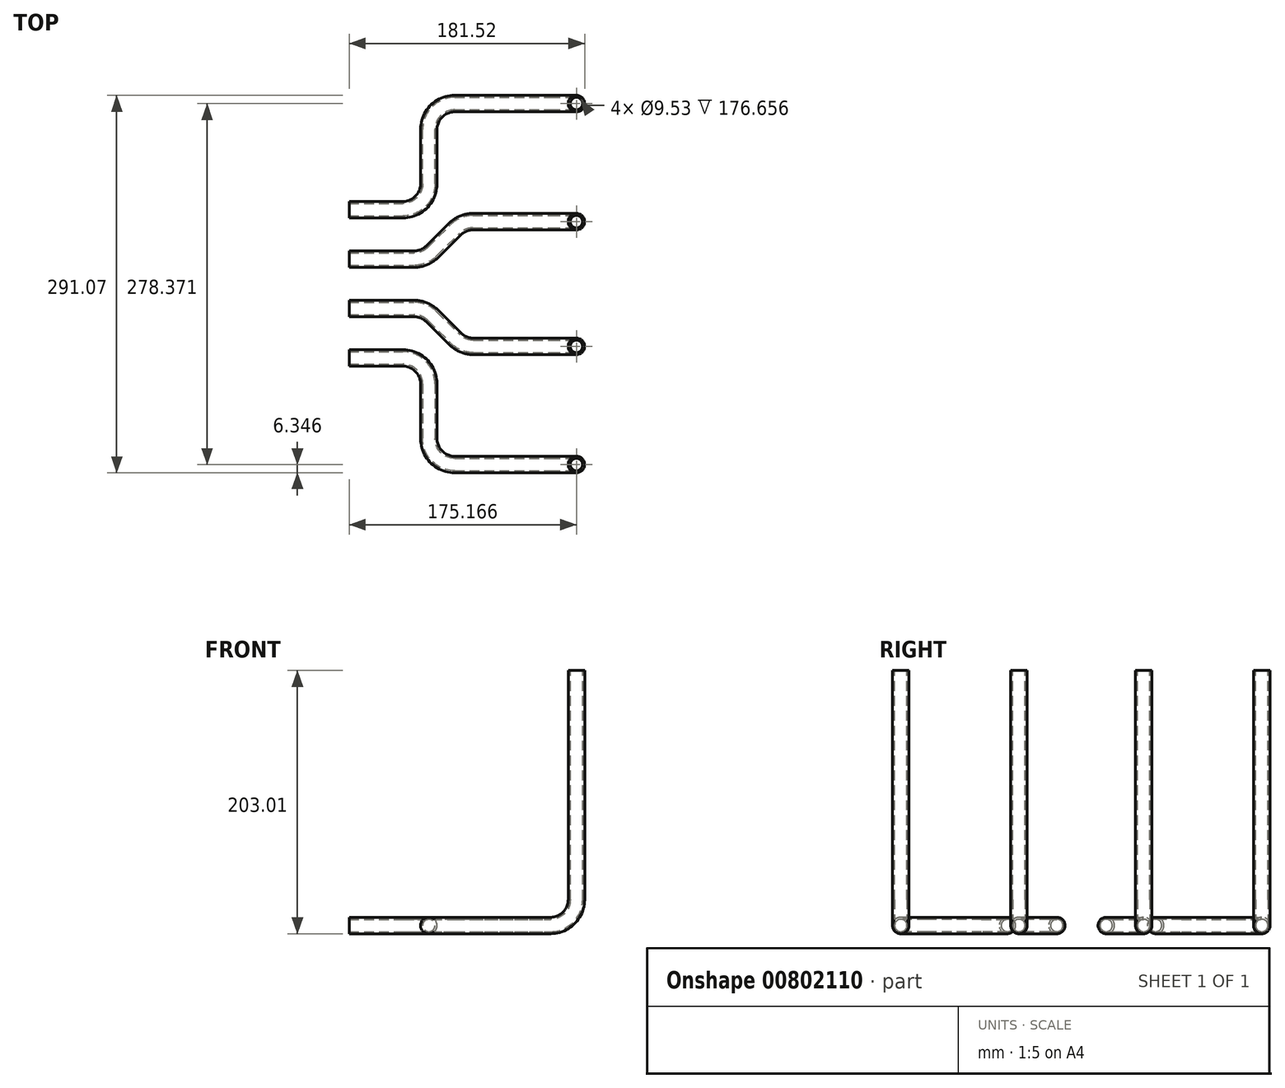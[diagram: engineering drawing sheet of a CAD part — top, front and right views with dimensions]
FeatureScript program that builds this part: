
annotation { "Feature Type Name" : "Feature", "Feature Type Description" : "" }
export const myFeature = defineFeature(function(context is Context, id is Id, definition is map)
    precondition{}
    {
        {
            var Q0;
            Q0=qCreatedBy(makeId("Front.planeOp"),FACE);
            cPlane(context, id + "F0", {"entities" : qUnion([Q0]), "cplaneType" : CPlaneType.OFFSET, "offset" : 158.4 * mm, "width" : 150 * mm, "height" : 150 * mm});
        }
        {
            var Q0;
            Q0=qCreatedBy(makeId("Top.planeOp"),FACE);
            var sketch = newSketch(context, id + "F1", { "sketchPlane" : qUnion([Q0])});
            skLineSegment(sketch, "E0", {"start": v(0, 0) * mm, "end": v(50, 0) * mm});
            skLineSegment(sketch, "E1", {"start": v(140, 28.88) * mm, "end": v(95.45, 28.88) * mm});
            skLineSegment(sketch, "E2", {"start": v(64.14, 5.86) * mm, "end": v(81.31, 23.03) * mm});
            skArc(sketch, "E3.filletArc", {"start": v(50, 0) * mm, "mid": v(57.65, 1.52) * mm, "end": v(64.14, 5.86) * mm});
            skArc(sketch, "E4.filletArc", {"start": v(95.45, 28.88) * mm, "mid": v(87.8, 27.36) * mm, "end": v(81.31, 23.03) * mm});
            skSolve(sketch);
        }
        {
            var Q0;
            Q0=qCreatedBy(makeId("Right.planeOp"),FACE);
            var sketch = newSketch(context, id + "F2", { "sketchPlane" : qUnion([Q0])});
            skCircle(sketch, "E5", {"center": v(0, 0) * mm, "radius": 6.35 * mm});
            skCircle(sketch, "E6", {"center": v(0, 0) * mm, "radius": 4.76 * mm});
            skSolve(sketch);
        }
        {
            var Q0;
            Q0=qCreatedBy(makeId("Front.planeOp"),FACE);
            cPlane(context, id + "F3", {"entities" : qUnion([Q0]), "cplaneType" : CPlaneType.OFFSET, "offset" : 28.89 * mm, "oppositeDirection" : true, "width" : 150 * mm, "height" : 150 * mm});
        }
        {
            var Q0;
            Q0=qCreatedBy(id+"F3.planeOp",FACE);
            var sketch = newSketch(context, id + "F4", { "sketchPlane" : qUnion([Q0])});
            skLineSegment(sketch, "E7", {"start": v(175.17, 196.66) * mm, "end": v(175.17, 20) * mm});
            skLineSegment(sketch, "E8", {"start": v(155.17, 0) * mm, "end": v(140, 0) * mm});
            skPoint(sketch, "E9.visualSharp", {"position": v(175.17, 0) * mm});
            skArc(sketch, "E9.filletArc", {"start": v(155.17, 0) * mm, "mid": v(169.3, 5.86) * mm, "end": v(175.17, 20) * mm});
            skSolve(sketch);
        }
        {
            var Q0;
            Q0=qSketchRegion(id+"F2",true);
            var Q1;
            Q1=qConstructionFilter(qBodyType(qCreatedBy(id+"F1",EDGE),BodyType.WIRE),ConstructionObject.NO);
            var Q2;
            Q2=qConstructionFilter(qBodyType(qCreatedBy(id+"F4",EDGE),BodyType.WIRE),ConstructionObject.NO);
            sweep(context, id + "F5", {"profiles" : qUnion([Q0]), "path" : qUnion([Q1, Q2])});
        }
        {
            var Q0;
            Q0=qCreatedBy(makeId("Right.planeOp"),FACE);
            var sketch = newSketch(context, id + "F6", { "sketchPlane" : qUnion([Q0])});
            skCircle(sketch, "E10", {"center": v(38.1, 0) * mm, "radius": 6.35 * mm});
            skCircle(sketch, "E11", {"center": v(38.1, 0) * mm, "radius": 4.76 * mm});
            skSolve(sketch);
        }
        {
            var Q0;
            Q0=qCreatedBy(makeId("Top.planeOp"),FACE);
            var sketch = newSketch(context, id + "F7", { "sketchPlane" : qUnion([Q0])});
            skLineSegment(sketch, "E12", {"start": v(0, 38.1) * mm, "end": v(41.35, 38.1) * mm});
            skLineSegment(sketch, "E13", {"start": v(61.35, 58.1) * mm, "end": v(61.35, 99.97) * mm});
            skLineSegment(sketch, "E14", {"start": v(81.35, 119.97) * mm, "end": v(155.17, 119.97) * mm});
            skPoint(sketch, "E15.visualSharp", {"position": v(61.35, 38.1) * mm});
            skArc(sketch, "E15.filletArc", {"start": v(41.35, 38.1) * mm, "mid": v(55.5, 43.96) * mm, "end": v(61.35, 58.1) * mm});
            skPoint(sketch, "E16.visualSharp", {"position": v(61.35, 119.97) * mm});
            skArc(sketch, "E16.filletArc", {"start": v(81.35, 119.97) * mm, "mid": v(67.21, 114.1) * mm, "end": v(61.35, 99.97) * mm});
            skSolve(sketch);
        }
        {
            var Q0;
            Q0=qCreatedBy(makeId("Front.planeOp"),FACE);
            cPlane(context, id + "F8", {"entities" : qUnion([Q0]), "cplaneType" : CPlaneType.OFFSET, "offset" : 119.97 * mm, "oppositeDirection" : true, "width" : 150 * mm, "height" : 150 * mm});
        }
        {
            var Q0;
            Q0=qCreatedBy(id+"F8.planeOp",FACE);
            var sketch = newSketch(context, id + "F9", { "sketchPlane" : qUnion([Q0])});
            skLineSegment(sketch, "E17", {"start": v(175.17, 196.66) * mm, "end": v(175.17, 20) * mm});
            skLineSegment(sketch, "E18", {"start": v(155.17, 0) * mm, "end": v(155.17, 0) * mm});
            skPoint(sketch, "E19.visualSharp", {"position": v(175.17, 0) * mm});
            skArc(sketch, "E19.filletArc", {"start": v(155.17, 0) * mm, "mid": v(169.3, 5.86) * mm, "end": v(175.17, 20) * mm});
            skSolve(sketch);
        }
        {
            var Q0;
            Q0=qCreatedBy(makeId("Right.planeOp"),FACE);
            var sketch = newSketch(context, id + "F10", { "sketchPlane" : qUnion([Q0])});
            skCircle(sketch, "E20", {"center": v(-38.1, 0) * mm, "radius": 6.35 * mm});
            skCircle(sketch, "E21", {"center": v(-38.1, 0) * mm, "radius": 4.76 * mm});
            skSolve(sketch);
        }
        {
            var Q0;
            Q0=qCreatedBy(makeId("Top.planeOp"),FACE);
            var sketch = newSketch(context, id + "F11", { "sketchPlane" : qUnion([Q0])});
            skLineSegment(sketch, "E22", {"start": v(0, -38.1) * mm, "end": v(50, -38.1) * mm});
            skLineSegment(sketch, "E23", {"start": v(155.17, -67.32) * mm, "end": v(95.8, -67.32) * mm});
            skLineSegment(sketch, "E24", {"start": v(155.17, 28.88) * mm, "end": v(155.17, -138.29) * mm, "construction": true});
            skLineSegment(sketch, "E25", {"start": v(64.14, -43.96) * mm, "end": v(81.65, -61.46) * mm});
            skPoint(sketch, "E26.newPointA", {"position": v(58.31, -38.1) * mm});
            skPoint(sketch, "E26.newPointB", {"position": v(58.31, -38.13) * mm});
            skArc(sketch, "E26.filletArc", {"start": v(64.14, -43.96) * mm, "mid": v(57.65, -39.62) * mm, "end": v(50, -38.1) * mm});
            skArc(sketch, "E27.filletArc", {"start": v(81.65, -61.46) * mm, "mid": v(88.14, -65.8) * mm, "end": v(95.8, -67.32) * mm});
            skSolve(sketch);
        }
        {
            var Q0;
            Q0=qCreatedBy(makeId("Front.planeOp"),FACE);
            cPlane(context, id + "F12", {"entities" : qUnion([Q0]), "cplaneType" : CPlaneType.OFFSET, "offset" : 67.32 * mm, "width" : 150 * mm, "height" : 150 * mm});
        }
        {
            var Q0;
            Q0=qCreatedBy(id+"F12.planeOp",FACE);
            var sketch = newSketch(context, id + "F13", { "sketchPlane" : qUnion([Q0])});
            skLineSegment(sketch, "E28", {"start": v(175.17, 196.66) * mm, "end": v(175.17, 20) * mm});
            skLineSegment(sketch, "E29", {"start": v(155.17, 0) * mm, "end": v(155.17, 0) * mm});
            skPoint(sketch, "E30.visualSharp", {"position": v(175.17, 0) * mm});
            skArc(sketch, "E30.filletArc", {"start": v(155.17, 0) * mm, "mid": v(169.3, 5.86) * mm, "end": v(175.17, 20) * mm});
            skSolve(sketch);
        }
        {
            var Q0;
            Q0=qSketchRegion(id+"F6",true);
            var Q1;
            Q1=qConstructionFilter(qBodyType(qCreatedBy(id+"F7",EDGE),BodyType.WIRE),ConstructionObject.NO);
            var Q2;
            Q2=qConstructionFilter(qBodyType(qCreatedBy(id+"F9",EDGE),BodyType.WIRE),ConstructionObject.NO);
            sweep(context, id + "F14", {"profiles" : qUnion([Q0]), "path" : qUnion([Q1, Q2])});
        }
        {
            var Q0;
            Q0=qSketchRegion(id+"F10",true);
            var Q1;
            Q1=qConstructionFilter(qBodyType(qCreatedBy(id+"F11",EDGE),BodyType.WIRE),ConstructionObject.NO);
            var Q2;
            Q2=qConstructionFilter(qBodyType(qCreatedBy(id+"F13",EDGE),BodyType.WIRE),ConstructionObject.NO);
            sweep(context, id + "F15", {"profiles" : qUnion([Q0]), "path" : qUnion([Q1, Q2])});
        }
        {
            var Q0;
            Q0=qCreatedBy(makeId("Right.planeOp"),FACE);
            var sketch = newSketch(context, id + "F16", { "sketchPlane" : qUnion([Q0])});
            skCircle(sketch, "E31", {"center": v(-76.2, 0) * mm, "radius": 6.35 * mm});
            skCircle(sketch, "E32", {"center": v(-76.2, 0) * mm, "radius": 4.76 * mm});
            skSolve(sketch);
        }
        {
            var Q0;
            Q0=qCreatedBy(makeId("Top.planeOp"),FACE);
            var sketch = newSketch(context, id + "F17", { "sketchPlane" : qUnion([Q0])});
            skLineSegment(sketch, "E33", {"start": v(0, -76.2) * mm, "end": v(41.35, -76.2) * mm});
            skLineSegment(sketch, "E34", {"start": v(41.35, 23.23) * mm, "end": v(41.35, -123.33) * mm, "construction": true});
            skLineSegment(sketch, "E35", {"start": v(61.35, -96.2) * mm, "end": v(61.35, -138.4) * mm});
            skArc(sketch, "E36.filletArc", {"start": v(61.35, -96.2) * mm, "mid": v(55.5, -82.06) * mm, "end": v(41.35, -76.2) * mm});
            skLineSegment(sketch, "E37", {"start": v(81.35, -158.4) * mm, "end": v(155.17, -158.4) * mm});
            skArc(sketch, "E38.filletArc", {"start": v(61.35, -138.4) * mm, "mid": v(67.21, -152.55) * mm, "end": v(81.35, -158.4) * mm});
            skSolve(sketch);
        }
        {
            var Q0;
            Q0=qCreatedBy(id+"F0.planeOp",FACE);
            var sketch = newSketch(context, id + "F18", { "sketchPlane" : qUnion([Q0])});
            skLineSegment(sketch, "E39", {"start": v(175.17, 196.66) * mm, "end": v(175.17, 20) * mm});
            skLineSegment(sketch, "E40", {"start": v(155.17, 0) * mm, "end": v(155.17, 0) * mm});
            skPoint(sketch, "E41.newPointA", {"position": v(175.17, 0) * mm});
            skArc(sketch, "E41.filletArc", {"start": v(155.17, 0) * mm, "mid": v(169.3, 5.86) * mm, "end": v(175.17, 20) * mm});
            skSolve(sketch);
        }
        {
            var Q0;
            Q0=qSketchRegion(id+"F16",true);
            var Q1;
            Q1=qConstructionFilter(qBodyType(qCreatedBy(id+"F17",EDGE),BodyType.WIRE),ConstructionObject.NO);
            var Q2;
            Q2=qConstructionFilter(qBodyType(qCreatedBy(id+"F18",EDGE),BodyType.WIRE),ConstructionObject.NO);
            sweep(context, id + "F19", {"profiles" : qUnion([Q0]), "path" : qUnion([Q1, Q2])});
        }
    });
